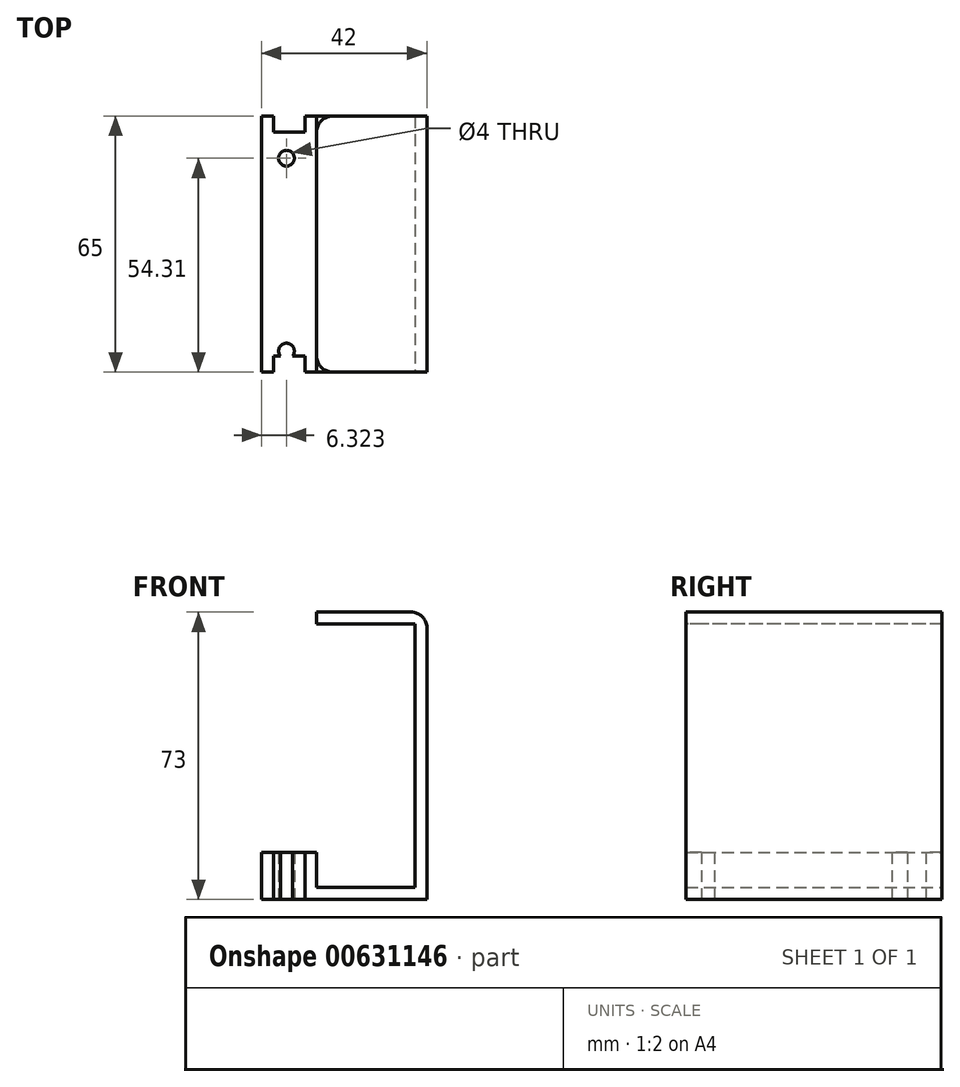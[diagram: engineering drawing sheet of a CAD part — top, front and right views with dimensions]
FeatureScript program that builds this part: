
annotation { "Feature Type Name" : "Feature", "Feature Type Description" : "" }
export const myFeature = defineFeature(function(context is Context, id is Id, definition is map)
    precondition{}
    {
        {
            var Q0;
            Q0=qCreatedBy(makeId("Top.planeOp"),FACE);
            var sketch = newSketch(context, id + "F0", { "sketchPlane" : qUnion([Q0])});
            skLineSegment(sketch, "E0", {"start": v(-28.2, 35.19) * mm, "end": v(-28.2, -29.81) * mm});
            skLineSegment(sketch, "E1", {"start": v(-28.2, -29.81) * mm, "end": v(-25.2, -29.81) * mm});
            skLineSegment(sketch, "E2", {"start": v(-25.2, -29.81) * mm, "end": v(-25.2, -25.81) * mm});
            skLineSegment(sketch, "E3", {"start": v(-25.2, -25.81) * mm, "end": v(-17.2, -25.81) * mm});
            skLineSegment(sketch, "E4", {"start": v(-17.2, -25.81) * mm, "end": v(-17.2, -29.81) * mm});
            skLineSegment(sketch, "E5", {"start": v(-17.2, -29.81) * mm, "end": v(-14.2, -29.81) * mm});
            skLineSegment(sketch, "E6", {"start": v(-14.2, -29.81) * mm, "end": v(-14.2, 35.19) * mm});
            skLineSegment(sketch, "E7", {"start": v(-14.2, 35.19) * mm, "end": v(-17.2, 35.19) * mm});
            skLineSegment(sketch, "E8", {"start": v(-17.2, 35.19) * mm, "end": v(-17.2, 31.19) * mm});
            skLineSegment(sketch, "E9", {"start": v(-17.2, 31.19) * mm, "end": v(-25.2, 31.19) * mm});
            skLineSegment(sketch, "E10", {"start": v(-25.2, 31.19) * mm, "end": v(-25.2, 35.19) * mm});
            skLineSegment(sketch, "E11", {"start": v(-25.2, 35.19) * mm, "end": v(-28.2, 35.19) * mm});
            skLineSegment(sketch, "E12", {"start": v(-14.2, -29.81) * mm, "end": v(13.8, -29.81) * mm});
            skLineSegment(sketch, "E13", {"start": v(13.8, -29.81) * mm, "end": v(13.8, 35.19) * mm});
            skLineSegment(sketch, "E14", {"start": v(13.8, 35.19) * mm, "end": v(-14.2, 35.19) * mm});
            skLineSegment(sketch, "E15", {"start": v(13.8, 35.19) * mm, "end": v(10.8, 35.19) * mm});
            skLineSegment(sketch, "E16", {"start": v(10.8, 35.19) * mm, "end": v(10.8, -29.81) * mm});
            skLineSegment(sketch, "E17", {"start": v(10.8, -29.81) * mm, "end": v(13.8, -29.81) * mm});
            skCircle(sketch, "E18", {"center": v(-21.87, 24.5) * mm, "radius": 2 * mm});
            skCircle(sketch, "E19", {"center": v(-21.87, -24.5) * mm, "radius": 2 * mm});
            skSolve(sketch);
        }
        {
            var Q0;
            Q0=makeQuery(id+"F0.imprint","IMPRINT",FACE,{"disambiguationData":[TD([[makeQuery(id+"F0.imprint","IMPRINT",EDGE,{"derivedFrom":sQuery(id+"F0.wireOp",EDGE,"E0")}),1.0]])]});
            extrude(context, id + "F1", {"entities" : qUnion([Q0]), "depth" : 12 * mm, "offsetDistance" : 25 * mm});
        }
        {
            var Q0;
            Q0=makeQuery(id+"F0.imprint","IMPRINT",FACE,{"disambiguationData":[TD([[makeQuery(id+"F0.imprint","IMPRINT",EDGE,{"derivedFrom":sQuery(id+"F0.wireOp",EDGE,"E6")}),-1.0]])]});
            extrude(context, id + "F2", {"entities" : qUnion([Q0]), "operationType" : NewBodyOperationType.ADD, "depth" : 3 * mm, "offsetDistance" : 25 * mm});
        }
        {
            var Q0;
            Q0=makeQuery(id+"F0.imprint","IMPRINT",FACE,{"disambiguationData":[TD([[makeQuery(id+"F0.imprint","IMPRINT",EDGE,{"derivedFrom":sQuery(id+"F0.wireOp",EDGE,"E13")}),1.0]])]});
            extrude(context, id + "F3", {"entities" : qUnion([Q0]), "operationType" : NewBodyOperationType.ADD, "depth" : 70 * mm, "offsetDistance" : 25 * mm});
        }
        {
            var Q0;
            Q0=makeQuery(id+"F3.boolean.opBoolean","MERGE",FACE,{"derivedFrom":[makeQuery(id+"F2.boolean.opBoolean","MERGE",FACE,{"derivedFrom":[makeQuery(id+"F1.opExtrude","SWEPT_FACE",FACE,{"disambiguationData":[OSD([sQuery(id+"F0.wireOp",EDGE,"E5")])]}),makeQuery(id+"F2.opExtrude","SWEPT_FACE",FACE,{"disambiguationData":[OSD([sQuery(id+"F0.wireOp",EDGE,"E12")])]})]}),makeQuery(id+"F3.opExtrude","SWEPT_FACE",FACE,{"disambiguationData":[OSD([sQuery(id+"F0.wireOp",EDGE,"E17")])]})]});
            var sketch = newSketch(context, id + "F4", { "sketchPlane" : qUnion([Q0])});
            skLineSegment(sketch, "E20", {"start": v(13.8, 70) * mm, "end": v(-14.2, 70) * mm});
            skLineSegment(sketch, "E21", {"start": v(-14.2, 70) * mm, "end": v(-14.2, 73) * mm});
            skLineSegment(sketch, "E22", {"start": v(-14.2, 73) * mm, "end": v(13.8, 73) * mm});
            skLineSegment(sketch, "E23", {"start": v(13.8, 73) * mm, "end": v(13.8, 70) * mm});
            skSolve(sketch);
        }
        {
            var Q0;
            {var subQ0=sQuery(id+"F4.wireOp",EDGE,"E21");Q0=makeQuery(id+"F4.imprint","IMPRINT",FACE,{"disambiguationData":[TD([[makeQuery(id+"F4.imprint","IMPRINT",EDGE,{"derivedFrom":subQ0}),-1.0]])]});}
            extrude(context, id + "F5", {"entities" : qUnion([Q0]), "operationType" : NewBodyOperationType.ADD, "oppositeDirection" : true, "depth" : 65 * mm, "offsetDistance" : 25 * mm});
        }
        {
            var Q0;
            Q0=makeQuery(id+"F2.opExtrude","CAP_EDGE",EDGE,{"disambiguationData":[OSD([sQuery(id+"F0.wireOp",EDGE,"E16")])],"isStart":false});
            var Q1;
            Q1=makeQuery(id+"F3.opExtrude","CAP_EDGE",EDGE,{"disambiguationData":[OSD([sQuery(id+"F0.wireOp",EDGE,"E16")])],"isStart":false});
            var Q2;
            Q2=makeQuery(id+"F2.opExtrude","CAP_EDGE",EDGE,{"disambiguationData":[OSD([sQuery(id+"F0.wireOp",EDGE,"E6")])],"isStart":false});
            var Q3;
            Q3=makeQuery(id+"F5.opExtrude","SWEPT_EDGE",EDGE,{"disambiguationData":[OSD([sQuery(id+"F4.wireOp",EDGE,"E22"),sQuery(id+"F4.wireOp",EDGE,"E23")])]});
            var Q4;
            Q4=makeQuery(id+"F5.opExtrude","CAP_EDGE",EDGE,{"disambiguationData":[OSD([sQuery(id+"F4.wireOp",EDGE,"E21")])],"isStart":true});
            var Q5;
            Q5=makeQuery(id+"F5.opExtrude","CAP_EDGE",EDGE,{"disambiguationData":[OSD([sQuery(id+"F4.wireOp",EDGE,"E21")])],"isStart":false});
            fillet(context, id + "F6", {"entities" : qUnion([Q0, Q1, Q2, Q3, Q4, Q5]), "radius" : 4 * mm, "tangentPropagation" : true, "allowEdgeOverflow" : false});
        }
    });
